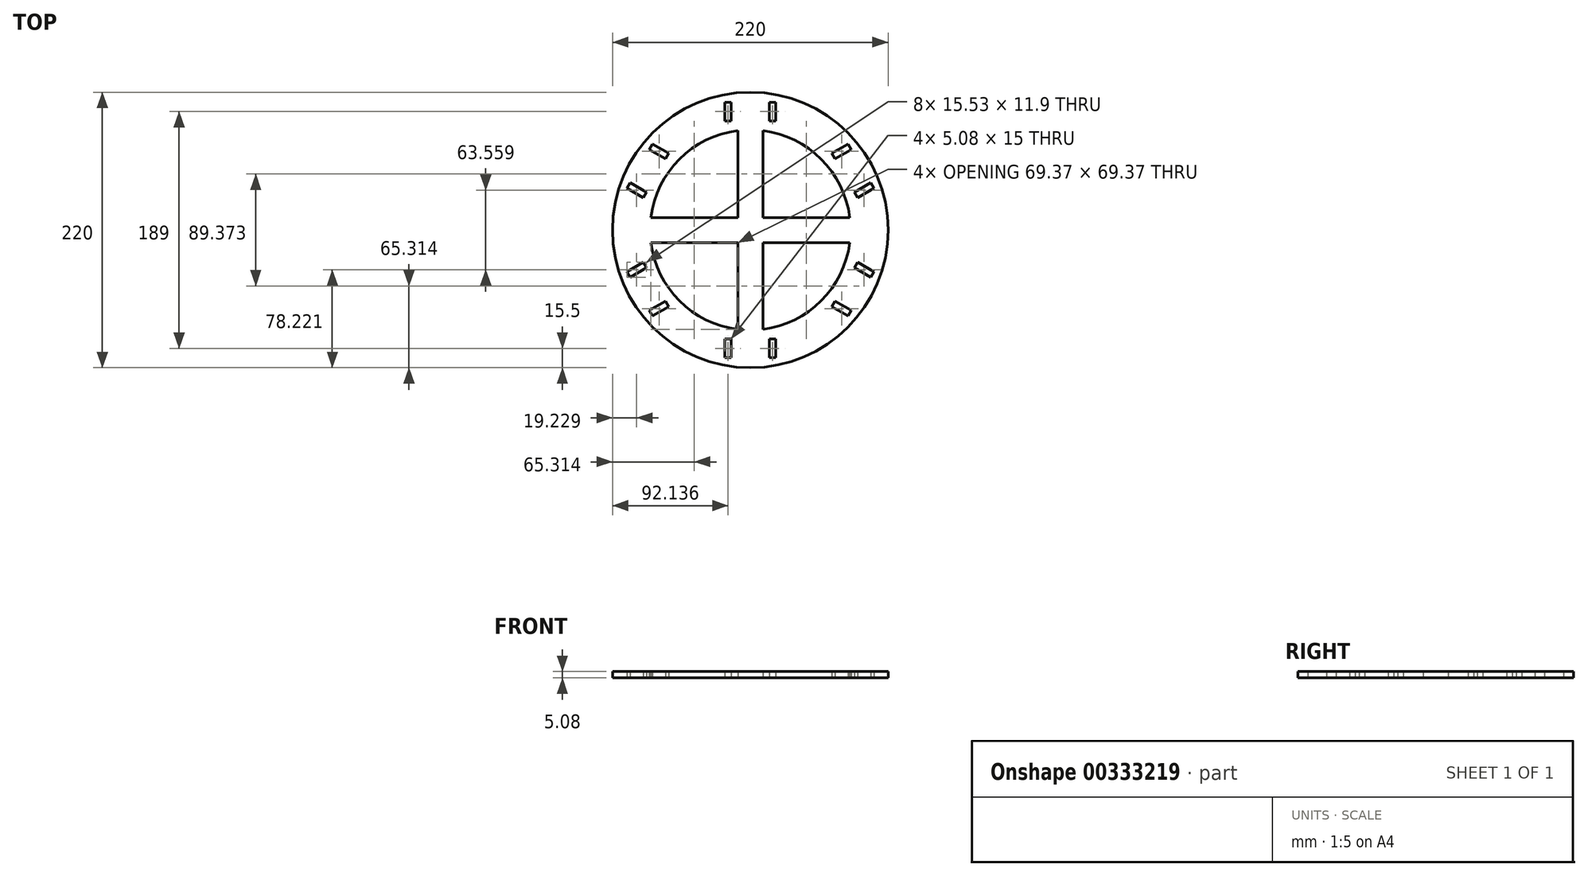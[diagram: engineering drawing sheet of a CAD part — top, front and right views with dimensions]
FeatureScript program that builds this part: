
annotation { "Feature Type Name" : "Feature", "Feature Type Description" : "" }
export const myFeature = defineFeature(function(context is Context, id is Id, definition is map)
    precondition{}
    {
        {
            var Q0;
            Q0=qCreatedBy(makeId("Top.planeOp"),FACE);
            var sketch = newSketch(context, id + "F0", { "sketchPlane" : qUnion([Q0])});
            skCircle(sketch, "E0", {"center": v(0, 0) * mm, "radius": 110 * mm});
            skArc(sketch, "E1", {"start": v(-10, 79.37) * mm, "mid": v(-56.57, 56.57) * mm, "end": v(-79.37, 10) * mm});
            skLineSegment(sketch, "E2.bottom", {"start": v(-20.4, 102) * mm, "end": v(-15.32, 102) * mm});
            skLineSegment(sketch, "E2.top", {"start": v(-20.4, 87) * mm, "end": v(-15.32, 87) * mm});
            skLineSegment(sketch, "E2.left", {"start": v(-20.4, 102) * mm, "end": v(-20.4, 87) * mm});
            skLineSegment(sketch, "E2.right", {"start": v(-15.32, 102) * mm, "end": v(-15.32, 87) * mm});
            skLineSegment(sketch, "E3", {"start": v(0, 0) * mm, "end": v(0, 117.32) * mm, "construction": true});
            skLineSegment(sketch, "E4.MirrorCS", {"start": v(15.32, 102) * mm, "end": v(15.32, 87) * mm});
            skLineSegment(sketch, "E5.MirrorCS", {"start": v(20.4, 102) * mm, "end": v(15.32, 102) * mm});
            skLineSegment(sketch, "E6.MirrorCS", {"start": v(20.4, 102) * mm, "end": v(20.4, 87) * mm});
            skLineSegment(sketch, "E7.MirrorCS", {"start": v(20.4, 87) * mm, "end": v(15.32, 87) * mm});
            skLineSegment(sketch, "E8.1.0", {"start": v(-98.54, 33.33) * mm, "end": v(-96, 37.73) * mm});
            skLineSegment(sketch, "E8.1.1", {"start": v(-98.54, 33.33) * mm, "end": v(-85.55, 25.83) * mm});
            skLineSegment(sketch, "E8.1.2", {"start": v(-85.55, 25.83) * mm, "end": v(-83, 30.23) * mm});
            skLineSegment(sketch, "E8.1.3", {"start": v(-96, 37.73) * mm, "end": v(-83, 30.23) * mm});
            skLineSegment(sketch, "E8.1.4", {"start": v(-80.67, 64.27) * mm, "end": v(-67.68, 56.77) * mm});
            skLineSegment(sketch, "E8.1.5", {"start": v(-78.13, 68.67) * mm, "end": v(-80.67, 64.27) * mm});
            skLineSegment(sketch, "E8.1.6", {"start": v(-78.13, 68.67) * mm, "end": v(-65.14, 61.17) * mm});
            skLineSegment(sketch, "E8.1.7", {"start": v(-65.14, 61.17) * mm, "end": v(-67.68, 56.77) * mm});
            skLineSegment(sketch, "E8.2.0", {"start": v(-78.13, -68.67) * mm, "end": v(-80.67, -64.27) * mm});
            skLineSegment(sketch, "E8.2.1", {"start": v(-78.13, -68.67) * mm, "end": v(-65.14, -61.17) * mm});
            skLineSegment(sketch, "E8.2.2", {"start": v(-65.14, -61.17) * mm, "end": v(-67.68, -56.77) * mm});
            skLineSegment(sketch, "E8.2.3", {"start": v(-80.67, -64.27) * mm, "end": v(-67.68, -56.77) * mm});
            skLineSegment(sketch, "E8.2.4", {"start": v(-96, -37.73) * mm, "end": v(-83, -30.23) * mm});
            skLineSegment(sketch, "E8.2.5", {"start": v(-98.54, -33.33) * mm, "end": v(-96, -37.73) * mm});
            skLineSegment(sketch, "E8.2.6", {"start": v(-98.54, -33.33) * mm, "end": v(-85.55, -25.83) * mm});
            skLineSegment(sketch, "E8.2.7", {"start": v(-85.55, -25.83) * mm, "end": v(-83, -30.23) * mm});
            skLineSegment(sketch, "E8.3.0", {"start": v(20.4, -102) * mm, "end": v(15.32, -102) * mm});
            skLineSegment(sketch, "E8.3.1", {"start": v(20.4, -102) * mm, "end": v(20.4, -87) * mm});
            skLineSegment(sketch, "E8.3.2", {"start": v(20.4, -87) * mm, "end": v(15.32, -87) * mm});
            skLineSegment(sketch, "E8.3.3", {"start": v(15.32, -102) * mm, "end": v(15.32, -87) * mm});
            skLineSegment(sketch, "E8.3.4", {"start": v(-15.32, -102) * mm, "end": v(-15.32, -87) * mm});
            skLineSegment(sketch, "E8.3.5", {"start": v(-20.4, -102) * mm, "end": v(-15.32, -102) * mm});
            skLineSegment(sketch, "E8.3.6", {"start": v(-20.4, -102) * mm, "end": v(-20.4, -87) * mm});
            skLineSegment(sketch, "E8.3.7", {"start": v(-20.4, -87) * mm, "end": v(-15.32, -87) * mm});
            skLineSegment(sketch, "E8.4.0", {"start": v(98.54, -33.33) * mm, "end": v(96, -37.73) * mm});
            skLineSegment(sketch, "E8.4.1", {"start": v(98.54, -33.33) * mm, "end": v(85.55, -25.83) * mm});
            skLineSegment(sketch, "E8.4.2", {"start": v(85.55, -25.83) * mm, "end": v(83, -30.23) * mm});
            skLineSegment(sketch, "E8.4.3", {"start": v(96, -37.73) * mm, "end": v(83, -30.23) * mm});
            skLineSegment(sketch, "E8.4.4", {"start": v(80.67, -64.27) * mm, "end": v(67.68, -56.77) * mm});
            skLineSegment(sketch, "E8.4.5", {"start": v(78.13, -68.67) * mm, "end": v(80.67, -64.27) * mm});
            skLineSegment(sketch, "E8.4.6", {"start": v(78.13, -68.67) * mm, "end": v(65.14, -61.17) * mm});
            skLineSegment(sketch, "E8.4.7", {"start": v(65.14, -61.17) * mm, "end": v(67.68, -56.77) * mm});
            skLineSegment(sketch, "E8.5.0", {"start": v(78.13, 68.67) * mm, "end": v(80.67, 64.27) * mm});
            skLineSegment(sketch, "E8.5.1", {"start": v(78.13, 68.67) * mm, "end": v(65.14, 61.17) * mm});
            skLineSegment(sketch, "E8.5.2", {"start": v(65.14, 61.17) * mm, "end": v(67.68, 56.77) * mm});
            skLineSegment(sketch, "E8.5.3", {"start": v(80.67, 64.27) * mm, "end": v(67.68, 56.77) * mm});
            skLineSegment(sketch, "E8.5.4", {"start": v(96, 37.73) * mm, "end": v(83, 30.23) * mm});
            skLineSegment(sketch, "E8.5.5", {"start": v(98.54, 33.33) * mm, "end": v(96, 37.73) * mm});
            skLineSegment(sketch, "E8.5.6", {"start": v(98.54, 33.33) * mm, "end": v(85.55, 25.83) * mm});
            skLineSegment(sketch, "E8.5.7", {"start": v(85.55, 25.83) * mm, "end": v(83, 30.23) * mm});
            skLineSegment(sketch, "E9", {"start": v(-10, 79.37) * mm, "end": v(-10, 10) * mm});
            skLineSegment(sketch, "E10.MirrorCS", {"start": v(10, 79.37) * mm, "end": v(10, 10) * mm});
            skArc(sketch, "E11.trimOffspring", {"start": v(10, -79.37) * mm, "mid": v(56.57, -56.57) * mm, "end": v(79.37, -10) * mm});
            skLineSegment(sketch, "E12", {"start": v(-79.37, 10) * mm, "end": v(-10, 10) * mm});
            skLineSegment(sketch, "E13.MirrorCS", {"start": v(-79.37, -10) * mm, "end": v(-10, -10) * mm});
            skLineSegment(sketch, "E14.trimOffspring", {"start": v(-10, -10) * mm, "end": v(-10, -79.37) * mm});
            skLineSegment(sketch, "E15.trimOffspring", {"start": v(10, -10) * mm, "end": v(10, -79.37) * mm});
            skArc(sketch, "E16.trimOffspring", {"start": v(-79.37, -10) * mm, "mid": v(-56.57, -56.57) * mm, "end": v(-10, -79.37) * mm});
            skArc(sketch, "E17.trimOffspring", {"start": v(79.37, 10) * mm, "mid": v(56.57, 56.57) * mm, "end": v(10, 79.37) * mm});
            skLineSegment(sketch, "E18.trimOffspring", {"start": v(10, 10) * mm, "end": v(79.37, 10) * mm});
            skLineSegment(sketch, "E19.trimOffspring", {"start": v(10, -10) * mm, "end": v(79.37, -10) * mm});
            skSolve(sketch);
        }
        {
            var Q0;
            Q0=qSketchRegion(id+"F0",true);
            extrude(context, id + "F1", {"entities" : qUnion([Q0]), "depth" : 5.08 * mm});
        }
    });
